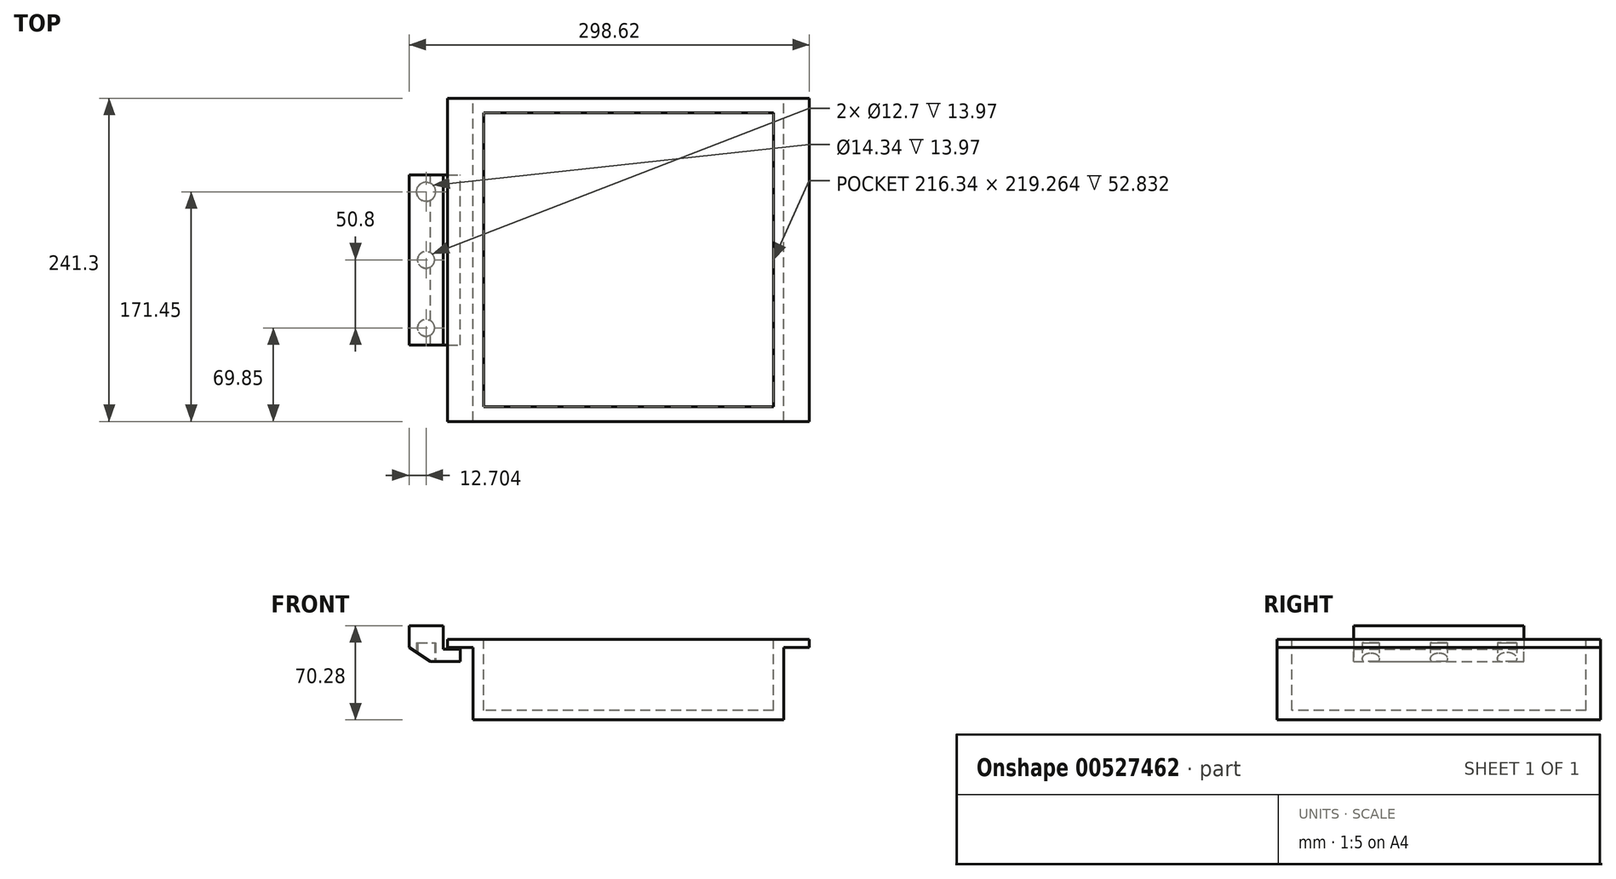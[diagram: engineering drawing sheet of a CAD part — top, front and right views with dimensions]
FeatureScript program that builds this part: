
annotation { "Feature Type Name" : "Feature", "Feature Type Description" : "" }
export const myFeature = defineFeature(function(context is Context, id is Id, definition is map)
    precondition{}
    {
        {
            var Q0;
            Q0=qCreatedBy(makeId("Front.planeOp"),FACE);
            var sketch = newSketch(context, id + "F0", { "sketchPlane" : qUnion([Q0])});
            skLineSegment(sketch, "E0.bottom", {"start": v(115.89, -54.24) * mm, "end": v(-115.89, -54.24) * mm});
            skLineSegment(sketch, "E0.top", {"start": v(115.89, 0) * mm, "end": v(-115.89, 0) * mm});
            skLineSegment(sketch, "E0.left", {"start": v(115.89, -54.24) * mm, "end": v(115.89, 0) * mm});
            skLineSegment(sketch, "E0.right", {"start": v(-115.89, -54.24) * mm, "end": v(-115.89, 0) * mm});
            skPoint(sketch, "E0.middle", {"position": v(0, -27.12) * mm});
            skLineSegment(sketch, "E1.bottom", {"start": v(134.94, 0) * mm, "end": v(-134.94, 0) * mm});
            skLineSegment(sketch, "E1.top", {"start": v(134.94, 5.75) * mm, "end": v(-134.94, 5.75) * mm});
            skLineSegment(sketch, "E1.left", {"start": v(134.94, 0) * mm, "end": v(134.94, 5.75) * mm});
            skLineSegment(sketch, "E1.right", {"start": v(-134.94, 0) * mm, "end": v(-134.94, 5.75) * mm});
            skPoint(sketch, "E1.middle", {"position": v(0, 2.87) * mm});
            skSolve(sketch);
        }
        {
            var Q0;
            Q0=qCreatedBy(makeId("Front.planeOp"),FACE);
            var sketch = newSketch(context, id + "F1", { "sketchPlane" : qUnion([Q0])});
            skLineSegment(sketch, "E2.bottom", {"start": v(-163.68, 16.04) * mm, "end": v(-138.28, 16.04) * mm});
            skLineSegment(sketch, "E2.top", {"start": v(-163.68, -10.7) * mm, "end": v(-138.28, -10.7) * mm});
            skLineSegment(sketch, "E2.left", {"start": v(-163.68, 16.04) * mm, "end": v(-163.68, -10.7) * mm});
            skLineSegment(sketch, "E2.right", {"start": v(-138.28, 16.04) * mm, "end": v(-138.28, -10.7) * mm});
            skLineSegment(sketch, "E3.bottom", {"start": v(-138.28, -10.7) * mm, "end": v(-125.58, -10.7) * mm});
            skLineSegment(sketch, "E3.top", {"start": v(-138.28, -1.4) * mm, "end": v(-125.58, -1.4) * mm});
            skLineSegment(sketch, "E3.left", {"start": v(-138.28, -10.7) * mm, "end": v(-138.28, -1.4) * mm});
            skLineSegment(sketch, "E3.right", {"start": v(-125.58, -10.7) * mm, "end": v(-125.58, -1.4) * mm});
            skSolve(sketch);
        }
        {
            var Q0;
            Q0=makeQuery(id+"F1.imprint","IMPRINT",FACE,{"disambiguationData":[TD([[makeQuery(id+"F1.imprint","IMPRINT",EDGE,{"derivedFrom":sQuery(id+"F1.wireOp",EDGE,"E2.bottom")}),-1.0]])]});
            var Q1;
            Q1=makeQuery(id+"F1.imprint","IMPRINT",FACE,{"disambiguationData":[TD([[makeQuery(id+"F1.imprint","IMPRINT",EDGE,{"derivedFrom":sQuery(id+"F1.wireOp",EDGE,"E3.bottom")}),1.0]])]});
            extrude(context, id + "F2", {"entities" : qUnion([Q0, Q1]), "endBound" : BoundingType.SYMMETRIC, "depth" : 127 * mm, "offsetDistance" : 25.4 * mm});
        }
        {
            var Q0;
            Q0=makeQuery(id+"F0.imprint","IMPRINT",FACE,{"disambiguationData":[TD([[makeQuery(id+"F0.imprint","IMPRINT",EDGE,{"derivedFrom":sQuery(id+"F0.wireOp",EDGE,"E1.top")}),1.0]])]});
            var Q1;
            Q1=makeQuery(id+"F0.imprint","IMPRINT",FACE,{"disambiguationData":[TD([[makeQuery(id+"F0.imprint","IMPRINT",EDGE,{"derivedFrom":sQuery(id+"F0.wireOp",EDGE,"E0.bottom")}),-1.0]])]});
            extrude(context, id + "F3", {"entities" : qUnion([Q0, Q1]), "endBound" : BoundingType.SYMMETRIC, "depth" : 241.3 * mm, "offsetDistance" : 25.4 * mm});
        }
        {
            var Q0;
            Q0=makeQuery(id+"F3.opExtrude","SWEPT_FACE",FACE,{"disambiguationData":[OSD([sQuery(id+"F0.wireOp",EDGE,"E1.top")])]});
            var sketch = newSketch(context, id + "F4", { "sketchPlane" : qUnion([Q0])});
            skLineSegment(sketch, "E4.bottom", {"start": v(108.17, 109.63) * mm, "end": v(-108.17, 109.63) * mm});
            skLineSegment(sketch, "E4.top", {"start": v(108.17, -109.63) * mm, "end": v(-108.17, -109.63) * mm});
            skLineSegment(sketch, "E4.left", {"start": v(108.17, 109.63) * mm, "end": v(108.17, -109.63) * mm});
            skLineSegment(sketch, "E4.right", {"start": v(-108.17, 109.63) * mm, "end": v(-108.17, -109.63) * mm});
            skPoint(sketch, "E4.middle", {"position": v(0, 0) * mm});
            skSolve(sketch);
        }
        {
            var Q0;
            Q0=makeQuery(id+"F4.imprint","IMPRINT",FACE,{"disambiguationData":[TD([[makeQuery(id+"F4.imprint","IMPRINT",EDGE,{"derivedFrom":sQuery(id+"F4.wireOp",EDGE,"E4.bottom")}),1.0]])]});
            extrude(context, id + "F5", {"entities" : qUnion([Q0]), "operationType" : NewBodyOperationType.REMOVE, "oppositeDirection" : true, "depth" : 52.83 * mm, "offsetDistance" : 25.4 * mm});
        }
        {
            var Q0;
            Q0=makeQuery(id+"F2.opExtrude","SWEPT_FACE",FACE,{"disambiguationData":[OSD([sQuery(id+"F1.wireOp",EDGE,"E2.top"),sQuery(id+"F1.wireOp",EDGE,"E3.bottom")])]});
            var sketch = newSketch(context, id + "F6", { "sketchPlane" : qUnion([Q0])});
            skLineSegment(sketch, "E5", {"start": v(-150.98, 63.5) * mm, "end": v(-150.98, -63.5) * mm});
            skPoint(sketch, "E6", {"position": v(-150.98, 50.8) * mm});
            skPoint(sketch, "E7", {"position": v(-150.98, 0) * mm});
            skPoint(sketch, "E8", {"position": v(-150.98, -50.8) * mm});
            skSolve(sketch);
        }
        {
            var Q0;
            Q0=makeQuery(id+"F2.opExtrude","CAP_FACE",FACE,{"disambiguationData":[OSD([sQuery(id+"F1.wireOp",EDGE,"E2.bottom"),sQuery(id+"F1.wireOp",EDGE,"E2.top"),sQuery(id+"F1.wireOp",EDGE,"E2.left"),sQuery(id+"F1.wireOp",EDGE,"E2.right"),sQuery(id+"F1.wireOp",EDGE,"E3.bottom"),sQuery(id+"F1.wireOp",EDGE,"E3.top"),sQuery(id+"F1.wireOp",EDGE,"E3.right")])],"isStart":true});
            var sketch = newSketch(context, id + "F7", { "sketchPlane" : qUnion([Q0])});
            skLineSegment(sketch, "E9.bottom", {"start": v(163.68, -10.7) * mm, "end": v(147.6, -10.7) * mm});
            skLineSegment(sketch, "E9.top", {"start": v(163.68, 0) * mm, "end": v(147.6, 0) * mm});
            skLineSegment(sketch, "E9.left", {"start": v(163.68, -10.7) * mm, "end": v(163.68, 0) * mm});
            skLineSegment(sketch, "E9.right", {"start": v(147.6, -10.7) * mm, "end": v(147.6, 0) * mm});
            skLineSegment(sketch, "E10", {"start": v(147.6, -10.7) * mm, "end": v(163.68, 0) * mm});
            skSolve(sketch);
        }
        {
            var Q0;
            Q0=makeQuery(id+"F7.imprint","IMPRINT",FACE,{"disambiguationData":[TD([[makeQuery(id+"F7.imprint","IMPRINT",EDGE,{"derivedFrom":sQuery(id+"F7.wireOp",EDGE,"E9.bottom")}),-1.0]])]});
            extrude(context, id + "F8", {"entities" : qUnion([Q0]), "operationType" : NewBodyOperationType.REMOVE, "endBound" : BoundingType.THROUGH_ALL, "oppositeDirection" : true, "depth" : 25.4 * mm, "offsetDistance" : 25.4 * mm});
        }
        {
            var Q0;
            {var subQ0=sQuery(id+"F6.wireOp",EDGE,"E5");Q0=makeQuery(id+"F6.imprint","IMPRINT",FACE,{"disambiguationData":[TD([[makeQuery(id+"F6.imprint","IMPRINT",EDGE,{"derivedFrom":subQ0}),1.0]])]});}
            var sketch = newSketch(context, id + "F9", { "sketchPlane" : qUnion([Q0])});
            skPoint(sketch, "E11.0", {"position": v(-150.98, 50.8) * mm});
            skPoint(sketch, "E12.0", {"position": v(-150.98, 0) * mm});
            skPoint(sketch, "E13.0", {"position": v(-150.98, -50.8) * mm});
            skCircle(sketch, "E14", {"center": v(-150.98, 50.8) * mm, "radius": 6.35 * mm});
            skCircle(sketch, "E15", {"center": v(-150.98, 0) * mm, "radius": 6.35 * mm});
            skCircle(sketch, "E16", {"center": v(-150.98, -50.8) * mm, "radius": 7.17 * mm});
            skSolve(sketch);
        }
        {
            var Q0;
            {var subQ0=sQuery(id+"F9.wireOp",EDGE,"E14");var subQ1=makeQuery(id+"F6.imprint","IMPRINT",EDGE,{"derivedFrom":sQuery(id+"F6.wireOp",EDGE,"E5")});var subQ2=makeQuery(id+"F9.imprint","INTERSECT",VERTEX,{"disambiguationData":[OD(0.0)],"derivedFrom":[subQ1,subQ0]});Q0=makeQuery(id+"F9.imprint","IMPRINT",FACE,{"disambiguationData":[TD([[makeQuery(id+"F9.imprint","IMPRINT",EDGE,{"disambiguationData":[TD([[subQ2,-1.0]])],"derivedFrom":subQ0}),1.0]])]});}
            var Q1;
            {var subQ0=sQuery(id+"F9.wireOp",EDGE,"E14");var subQ1=makeQuery(id+"F6.imprint","IMPRINT",EDGE,{"derivedFrom":sQuery(id+"F6.wireOp",EDGE,"E5")});var subQ2=makeQuery(id+"F9.imprint","INTERSECT",VERTEX,{"disambiguationData":[OD(0.0)],"derivedFrom":[subQ1,subQ0]});Q1=makeQuery(id+"F9.imprint","IMPRINT",FACE,{"disambiguationData":[TD([[makeQuery(id+"F9.imprint","IMPRINT",EDGE,{"disambiguationData":[TD([[subQ2,1.0]])],"derivedFrom":subQ0}),1.0]])]});}
            var Q2;
            {var subQ0=sQuery(id+"F9.wireOp",EDGE,"E15");var subQ1=makeQuery(id+"F6.imprint","IMPRINT",EDGE,{"derivedFrom":sQuery(id+"F6.wireOp",EDGE,"E5")});var subQ2=makeQuery(id+"F9.imprint","INTERSECT",VERTEX,{"disambiguationData":[OD(0.0)],"derivedFrom":[subQ1,subQ0]});Q2=makeQuery(id+"F9.imprint","IMPRINT",FACE,{"disambiguationData":[TD([[makeQuery(id+"F9.imprint","IMPRINT",EDGE,{"disambiguationData":[TD([[subQ2,1.0]])],"derivedFrom":subQ0}),1.0]])]});}
            var Q3;
            {var subQ0=sQuery(id+"F9.wireOp",EDGE,"E15");var subQ1=makeQuery(id+"F6.imprint","IMPRINT",EDGE,{"derivedFrom":sQuery(id+"F6.wireOp",EDGE,"E5")});var subQ2=makeQuery(id+"F9.imprint","INTERSECT",VERTEX,{"disambiguationData":[OD(0.0)],"derivedFrom":[subQ1,subQ0]});Q3=makeQuery(id+"F9.imprint","IMPRINT",FACE,{"disambiguationData":[TD([[makeQuery(id+"F9.imprint","IMPRINT",EDGE,{"disambiguationData":[TD([[subQ2,-1.0]])],"derivedFrom":subQ0}),1.0]])]});}
            var Q4;
            {var subQ0=sQuery(id+"F9.wireOp",EDGE,"E16");var subQ1=makeQuery(id+"F6.imprint","IMPRINT",EDGE,{"derivedFrom":sQuery(id+"F6.wireOp",EDGE,"E5")});var subQ2=makeQuery(id+"F9.imprint","INTERSECT",VERTEX,{"disambiguationData":[OD(0.0)],"derivedFrom":[subQ1,subQ0]});Q4=makeQuery(id+"F9.imprint","IMPRINT",FACE,{"disambiguationData":[TD([[makeQuery(id+"F9.imprint","IMPRINT",EDGE,{"disambiguationData":[TD([[subQ2,1.0]])],"derivedFrom":subQ0}),1.0]])]});}
            var Q5;
            {var subQ0=sQuery(id+"F9.wireOp",EDGE,"E16");var subQ1=makeQuery(id+"F6.imprint","IMPRINT",EDGE,{"derivedFrom":sQuery(id+"F6.wireOp",EDGE,"E5")});var subQ2=makeQuery(id+"F9.imprint","INTERSECT",VERTEX,{"disambiguationData":[OD(0.0)],"derivedFrom":[subQ1,subQ0]});Q5=makeQuery(id+"F9.imprint","IMPRINT",FACE,{"disambiguationData":[TD([[makeQuery(id+"F9.imprint","IMPRINT",EDGE,{"disambiguationData":[TD([[subQ2,-1.0]])],"derivedFrom":subQ0}),1.0]])]});}
            extrude(context, id + "F10", {"entities" : qUnion([Q0, Q1, Q2, Q3, Q4, Q5]), "operationType" : NewBodyOperationType.REMOVE, "oppositeDirection" : true, "depth" : 13.97 * mm, "offsetDistance" : 25.4 * mm});
        }
    });
